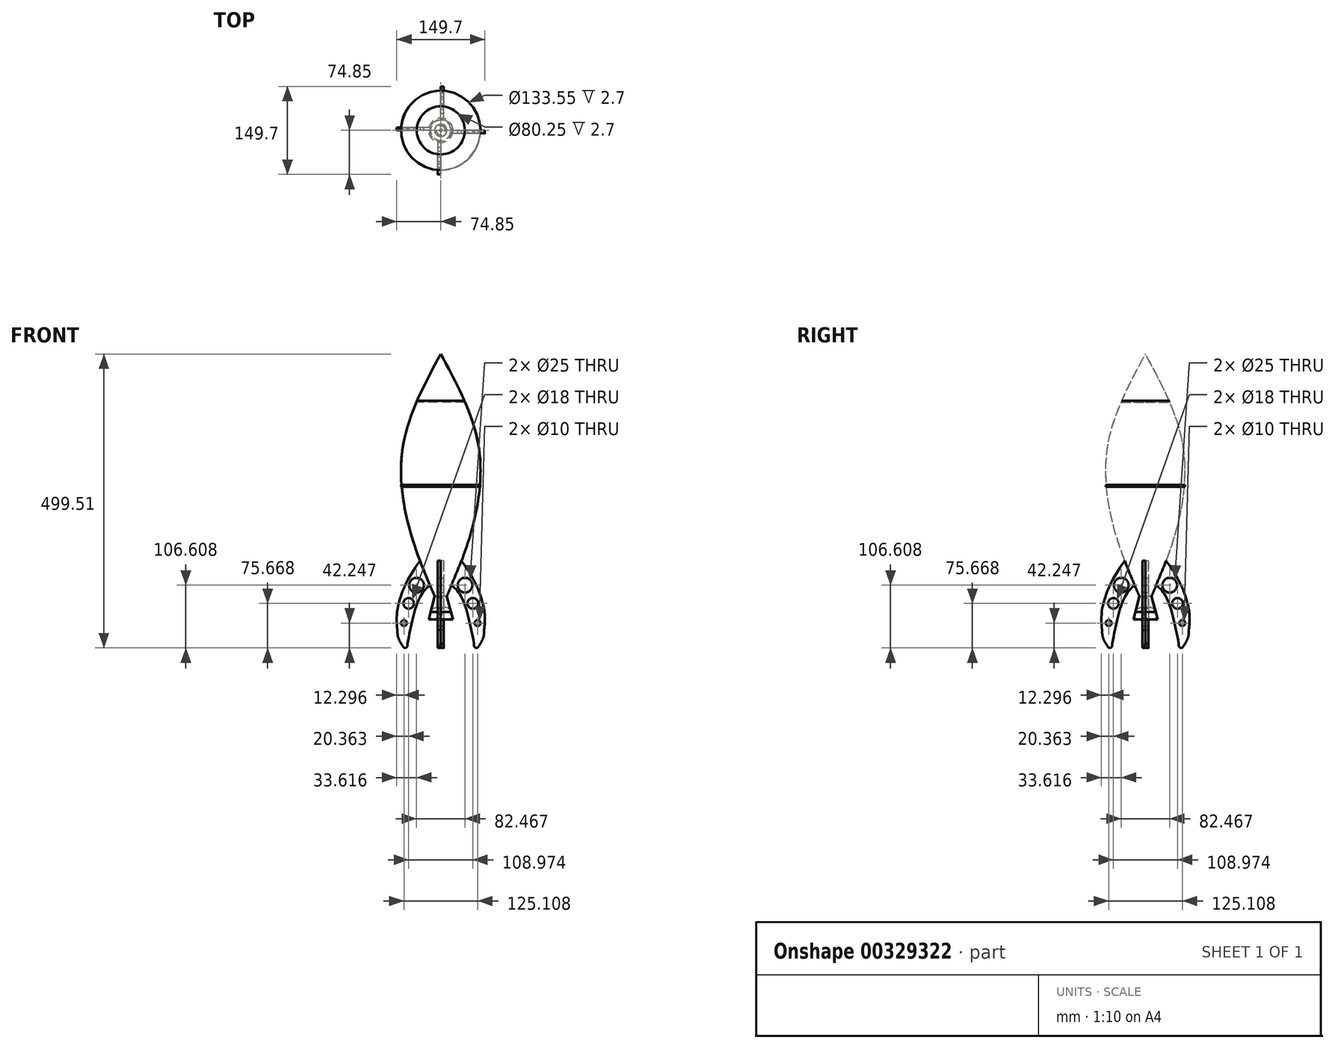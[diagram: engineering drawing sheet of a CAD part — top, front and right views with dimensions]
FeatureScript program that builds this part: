
annotation { "Feature Type Name" : "Feature", "Feature Type Description" : "" }
export const myFeature = defineFeature(function(context is Context, id is Id, definition is map)
    precondition{}
    {
        {
            var Q0;
            Q0=qCreatedBy(makeId("Right.planeOp"),FACE);
            var sketch = newSketch(context, id + "F0", { "sketchPlane" : qUnion([Q0])});
            skLineSegment(sketch, "E0", {"start": v(0, 0) * mm, "end": v(0, 225.45) * mm});
            skLineSegment(sketch, "E1.MirrorCS", {"start": v(0, 0) * mm, "end": v(0, -225.45) * mm});
            skLineSegment(sketch, "E2", {"start": v(0, -225.45) * mm, "end": v(20.65, -225.45) * mm});
            skLineSegment(sketch, "E3", {"start": v(20.65, -225.45) * mm, "end": v(10.2, -186.38) * mm});
            skPoint(sketch, "E4.visualSharp", {"position": v(64.27, 23.3) * mm});
            skFitSpline(sketch, "E5", {"points": [v(10.2, -186.38) * mm, v(51.3, -78.25) * mm, v(64.27, 68.99) * mm, v(0, 225.45) * mm], "startDerivative": vector(149, 342.41) * mm, "endDerivative": vector(-229.84, 425.91) * mm});
            skSolve(sketch);
        }
        {
            var Q0;
            Q0=makeQuery(id+"F0.imprint","IMPRINT",FACE,{"disambiguationData":[TD([[makeQuery(id+"F0.imprint","IMPRINT",EDGE,{"derivedFrom":sQuery(id+"F0.wireOp",EDGE,"E0")}),-1.0]])]});
            var Q1;
            Q1=sQuery(id+"F0.wireOp",EDGE,"E1.MirrorCS");
            revolve(context, id + "F1", {"entities" : qUnion([Q0]), "axis" : qUnion([Q1]), "revolveType" : RevolveType.FULL});
        }
        {
            var Q0;
            Q0=qCreatedBy(makeId("Right.planeOp"),FACE);
            var sketch = newSketch(context, id + "F2", { "sketchPlane" : qUnion([Q0])});
            skLineSegment(sketch, "E6", {"start": v(0, 0) * mm, "end": v(0, -186.1) * mm});
            skLineSegment(sketch, "E7", {"start": v(0, -93.05) * mm, "end": v(1.4, -93.05) * mm});
            skLineSegment(sketch, "E8", {"start": v(1.4, -93.05) * mm, "end": v(1.4, -113.4) * mm});
            skLineSegment(sketch, "E9", {"start": v(1.4, -113.4) * mm, "end": v(0, -113.4) * mm});
            skLineSegment(sketch, "E10.MirrorCS", {"start": v(-1.4, -93.05) * mm, "end": v(-1.4, -113.4) * mm});
            skLineSegment(sketch, "E11.MirrorCS", {"start": v(0, -93.05) * mm, "end": v(-1.4, -93.05) * mm});
            skLineSegment(sketch, "E12.MirrorCS", {"start": v(-1.4, -113.4) * mm, "end": v(0, -113.4) * mm});
            skFitSpline(sketch, "E13", {"points": [v(0, -93.05) * mm, v(15.8, -104.66) * mm, v(45.59, -140.8) * mm, v(66.32, -182.13) * mm, v(74.63, -217.65) * mm, v(72.15, -256.95) * mm], "startDerivative": vector(101.63, -63.9) * mm, "endDerivative": vector(-23.99, -193.86) * mm});
            skLineSegment(sketch, "E14", {"start": v(0, -113.4) * mm, "end": v(0, -134) * mm});
            skLineSegment(sketch, "E15", {"start": v(73.8, -243.6) * mm, "end": v(73.67, -243.98) * mm});
            skLineSegment(sketch, "E16", {"start": v(56.6, -270.06) * mm, "end": v(56.6, -267.14) * mm});
            skPoint(sketch, "E17.visualSharp", {"position": v(56.6, -294.3) * mm});
            skArc(sketch, "E17.filletArc", {"start": v(56.6, -270.06) * mm, "mid": v(59.94, -274) * mm, "end": v(64.38, -271.35) * mm});
            skLineSegment(sketch, "E18", {"start": v(0, -134) * mm, "end": v(0, -158.1) * mm});
            skFitSpline(sketch, "E19", {"points": [v(0, -158.1) * mm, v(30.23, -179.65) * mm, v(56.6, -267.14) * mm], "startDerivative": vector(84.36, -38.24) * mm, "endDerivative": vector(32.64, -170.09) * mm});
            skFitSpline(sketch, "E20", {"points": [v(73.8, -243.6) * mm, v(72.15, -256.95) * mm, v(64.38, -271.35) * mm], "startDerivative": vector(-0.78, -28.21) * mm, "endDerivative": vector(-17.78, -27.3) * mm});
            skSolve(sketch);
        }
        {
            var Q0;
            Q0 = qSketchRegion(id + "F2", true);
            extrude(context, id + "F3", {"entities" : qUnion([Q0]), "operationType" : NewBodyOperationType.ADD, "depth" : 5 * mm});
        }
        {
            var Q0;
            Q0=makeQuery(id+"F3.opExtrude","CAP_FACE",FACE,{"disambiguationData":[OSD([sQuery(id+"F2.wireOp",EDGE,"E7"),sQuery(id+"F2.wireOp",EDGE,"E8"),sQuery(id+"F2.wireOp",EDGE,"E10.MirrorCS"),sQuery(id+"F2.wireOp",EDGE,"E11.MirrorCS"),sQuery(id+"F2.wireOp",EDGE,"E12.MirrorCS"),sQuery(id+"F2.wireOp",EDGE,"E13"),sQuery(id+"F2.wireOp",EDGE,"E14"),sQuery(id+"F2.wireOp",EDGE,"7c6b737f-9552-418a-b940-284724824be0"),sQuery(id+"F2.wireOp",EDGE,"E15"),sQuery(id+"F2.wireOp",EDGE,"E16"),sQuery(id+"F2.wireOp",EDGE,"E17.filletArc")])],"isStart":false});
            var sketch = newSketch(context, id + "F4", { "sketchPlane" : qUnion([Q0])});
            skCircle(sketch, "E21", {"center": v(41.23, -167.45) * mm, "radius": 11.57 * mm});
            skSolve(sketch);
        }
        {
            var Q0;
            Q0=makeQuery(id+"F3.opExtrude","CAP_FACE",FACE,{"disambiguationData":[OSD([sQuery(id+"F2.wireOp",EDGE,"E7"),sQuery(id+"F2.wireOp",EDGE,"E8"),sQuery(id+"F2.wireOp",EDGE,"E10.MirrorCS"),sQuery(id+"F2.wireOp",EDGE,"E11.MirrorCS"),sQuery(id+"F2.wireOp",EDGE,"E12.MirrorCS"),sQuery(id+"F2.wireOp",EDGE,"E13"),sQuery(id+"F2.wireOp",EDGE,"E14"),sQuery(id+"F2.wireOp",EDGE,"7c6b737f-9552-418a-b940-284724824be0"),sQuery(id+"F2.wireOp",EDGE,"E15"),sQuery(id+"F2.wireOp",EDGE,"E16"),sQuery(id+"F2.wireOp",EDGE,"E17.filletArc")])],"isStart":false});
            var sketch = newSketch(context, id + "F5", { "sketchPlane" : qUnion([Q0])});
            skCircle(sketch, "E22", {"center": v(59.48, -192.02) * mm, "radius": 5.94 * mm});
            skSolve(sketch);
        }
        {
            var Q0;
            Q0=sQuery(id+"F4.wireOp",VERTEX,"E21.center");
            var Q1;
            Q1=makeQuery(id+"F1.opRevolve","SWEPT_BODY",BODY,{"disambiguationData":[OSD([sQuery(id+"F0.wireOp",EDGE,"E0"),sQuery(id+"F0.wireOp",EDGE,"E1.MirrorCS"),sQuery(id+"F0.wireOp",EDGE,"E2"),sQuery(id+"F0.wireOp",EDGE,"E3"),sQuery(id+"F0.wireOp",EDGE,"E5")])]});
            hole(context, id + "F6", {"style" : HoleStyle.SIMPLE, "endStyle" : HoleEndStyle.THROUGH, "holeDiameter" : 25 * mm, "tappedDepth" : 12 * mm, "tapClearance" : 3, "locations" : qUnion([Q0]), "scope" : qUnion([Q1])});
        }
        {
            var Q0;
            Q0=makeQuery(id+"F5.imprint","IMPRINT",FACE,{"disambiguationData":[TD([[makeQuery(id+"F5.imprint","IMPRINT",EDGE,{"derivedFrom":sQuery(id+"F5.wireOp",EDGE,"E22")}),-1.0]])]});
            var sketch = newSketch(context, id + "F7", { "sketchPlane" : qUnion([Q0])});
            skCircle(sketch, "E23", {"center": v(54.49, -198.4) * mm, "radius": 7.75 * mm});
            skSolve(sketch);
        }
        {
            var Q0;
            Q0=sQuery(id+"F7.wireOp",VERTEX,"E23.center");
            var Q1;
            Q1=makeQuery(id+"F1.opRevolve","SWEPT_BODY",BODY,{"disambiguationData":[OSD([sQuery(id+"F0.wireOp",EDGE,"E0"),sQuery(id+"F0.wireOp",EDGE,"E1.MirrorCS"),sQuery(id+"F0.wireOp",EDGE,"E2"),sQuery(id+"F0.wireOp",EDGE,"E3"),sQuery(id+"F0.wireOp",EDGE,"E5")])]});
            hole(context, id + "F8", {"style" : HoleStyle.SIMPLE, "endStyle" : HoleEndStyle.THROUGH, "holeDiameter" : 18 * mm, "tappedDepth" : 12 * mm, "tapClearance" : 3, "locations" : qUnion([Q0]), "scope" : qUnion([Q1])});
        }
        {
            var Q0;
            Q0=makeQuery(id+"F5.imprint","IMPRINT",FACE,{"disambiguationData":[TD([[makeQuery(id+"F5.imprint","IMPRINT",EDGE,{"derivedFrom":sQuery(id+"F5.wireOp",EDGE,"E22")}),-1.0]])]});
            var sketch = newSketch(context, id + "F9", { "sketchPlane" : qUnion([Q0])});
            skCircle(sketch, "E24", {"center": v(62.55, -231.81) * mm, "radius": 6.23 * mm});
            skSolve(sketch);
        }
        {
            var Q0;
            Q0=sQuery(id+"F9.wireOp",VERTEX,"E24.center");
            var Q1;
            Q1=makeQuery(id+"F1.opRevolve","SWEPT_BODY",BODY,{"disambiguationData":[OSD([sQuery(id+"F0.wireOp",EDGE,"E0"),sQuery(id+"F0.wireOp",EDGE,"E1.MirrorCS"),sQuery(id+"F0.wireOp",EDGE,"E2"),sQuery(id+"F0.wireOp",EDGE,"E3"),sQuery(id+"F0.wireOp",EDGE,"E5")])]});
            hole(context, id + "F10", {"style" : HoleStyle.SIMPLE, "endStyle" : HoleEndStyle.THROUGH, "holeDiameter" : 10 * mm, "tappedDepth" : 12 * mm, "tapClearance" : 3, "locations" : qUnion([Q0]), "scope" : qUnion([Q1])});
        }
        {
            var Q0;
            Q0=makeQuery(id+"F1.opRevolve","SWEPT_BODY",BODY,{"disambiguationData":[OSD([sQuery(id+"F0.wireOp",EDGE,"E0"),sQuery(id+"F0.wireOp",EDGE,"E1.MirrorCS"),sQuery(id+"F0.wireOp",EDGE,"E2"),sQuery(id+"F0.wireOp",EDGE,"E3"),sQuery(id+"F0.wireOp",EDGE,"E5")])]});
            var Q1;
            Q1=makeQuery(id+"F1.opRevolve","SWEPT_FACE",FACE,{"disambiguationData":[OSD([sQuery(id+"F0.wireOp",EDGE,"E5")])]});
            circularPattern(context, id + "F11", {"entities" : qUnion([Q0]), "axis" : qUnion([Q1]), "angle" : 360 * degree, "instanceCount" : 4, "equalSpace" : true});
        }
        {
            var Q0;
            Q0=qCreatedBy(makeId("Top.planeOp"),FACE);
            var sketch = newSketch(context, id + "F12", { "sketchPlane" : qUnion([Q0])});
            skCircle(sketch, "E25", {"center": v(0, 0) * mm, "radius": 67.47 * mm});
            skCircle(sketch, "E26", {"center": v(0, 0) * mm, "radius": 66.77 * mm});
            skSolve(sketch);
        }
        {
            var Q0;
            Q0 = qSketchRegion(id + "F12", true);
            extrude(context, id + "F13", {"entities" : qUnion([Q0]), "depth" : 2.7 * mm});
        }
        {
            var Q0;
            Q0=qCreatedBy(makeId("Top.planeOp"),FACE);
            cPlane(context, id + "F14", {"entities" : qUnion([Q0]), "cplaneType" : CPlaneType.OFFSET, "offset" : 143 * mm, "width" : 150 * mm, "height" : 150 * mm});
        }
        {
            var Q0;
            Q0=qCreatedBy(id+"F14.planeOp",FACE);
            var sketch = newSketch(context, id + "F15", { "sketchPlane" : qUnion([Q0])});
            skCircle(sketch, "E27", {"center": v(0, 0) * mm, "radius": 40.88 * mm});
            skCircle(sketch, "E28", {"center": v(0, 0) * mm, "radius": 40.13 * mm});
            skSolve(sketch);
        }
        {
            var Q0;
            Q0 = qSketchRegion(id + "F15", true);
            extrude(context, id + "F16", {"entities" : qUnion([Q0]), "depth" : 2.7 * mm});
        }
        {
            var Q0;
            Q0=makeQuery(id+"F11.opPattern","COPY",FACE,{"derivedFrom":makeQuery(id+"F1.opRevolve","SWEPT_FACE",FACE,{"disambiguationData":[OSD([sQuery(id+"F0.wireOp",EDGE,"E3")])]}),"instanceName":"2"});
            fillet(context, id + "F17", {"entities" : qUnion([Q0]), "radius" : 5.76 * mm, "tangentPropagation" : true, "allowEdgeOverflow" : false});
        }
        {
            var Q0;
            Q0=makeQuery(id+"F11.opPattern","COPY",FACE,{"derivedFrom":makeQuery(id+"F1.opRevolve","SWEPT_FACE",FACE,{"disambiguationData":[OSD([sQuery(id+"F0.wireOp",EDGE,"E2")])]}),"instanceName":"1"});
            fillet(context, id + "F18", {"entities" : qUnion([Q0]), "radius" : 9.97 * mm, "tangentPropagation" : true, "allowEdgeOverflow" : false});
        }
    });
